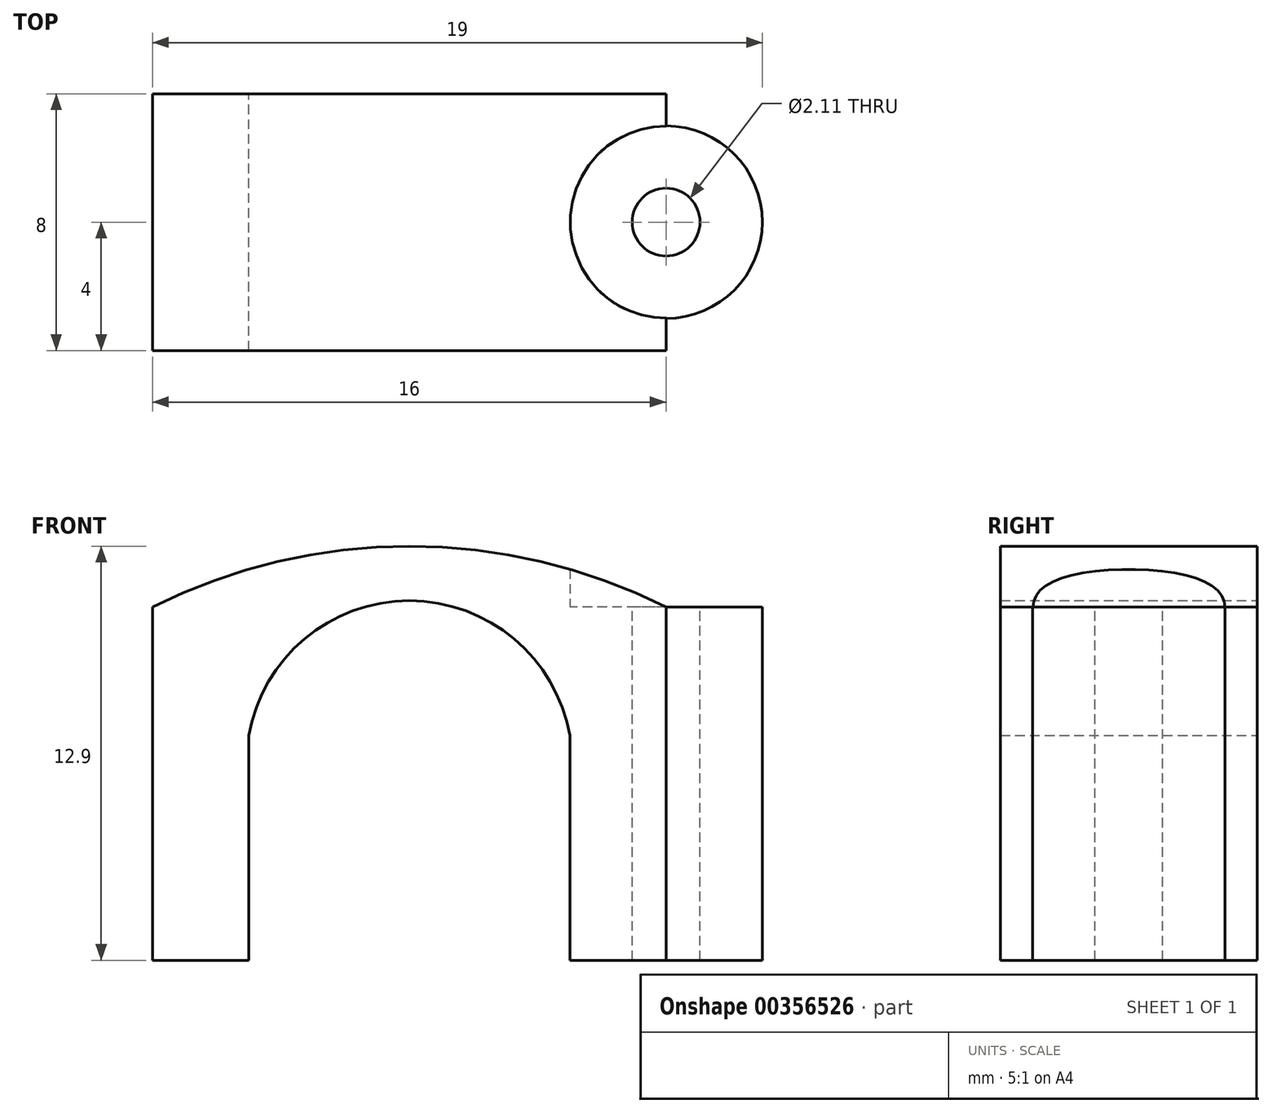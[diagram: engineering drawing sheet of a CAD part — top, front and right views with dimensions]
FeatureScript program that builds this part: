
annotation { "Feature Type Name" : "Feature", "Feature Type Description" : "" }
export const myFeature = defineFeature(function(context is Context, id is Id, definition is map)
    precondition{}
    {
        {
            var Q0;
            Q0=qCreatedBy(makeId("Top.planeOp"),FACE);
            var sketch = newSketch(context, id + "F0", { "sketchPlane" : qUnion([Q0])});
            skLineSegment(sketch, "E0.bottom", {"start": v(0, 0) * mm, "end": v(16, 0) * mm});
            skLineSegment(sketch, "E0.top", {"start": v(0, 8) * mm, "end": v(16, 8) * mm});
            skLineSegment(sketch, "E0.left", {"start": v(0, 0) * mm, "end": v(0, 8) * mm});
            skLineSegment(sketch, "E0.right", {"start": v(16, 0) * mm, "end": v(16, 8) * mm});
            skSolve(sketch);
        }
        {
            var Q0;
            Q0=makeQuery(id+"F0.imprint","IMPRINT",FACE,{"disambiguationData":[TD([[makeQuery(id+"F0.imprint","IMPRINT",EDGE,{"derivedFrom":sQuery(id+"F0.wireOp",EDGE,"E0.bottom")}),1.0]])]});
            extrude(context, id + "F1", {"entities" : qUnion([Q0]), "depth" : 11 * mm});
        }
        {
            var Q0;
            Q0=makeQuery(id+"F1.opExtrude","CAP_FACE",FACE,{"disambiguationData":[OSD([sQuery(id+"F0.wireOp",EDGE,"E0.bottom"),sQuery(id+"F0.wireOp",EDGE,"E0.top"),sQuery(id+"F0.wireOp",EDGE,"E0.left"),sQuery(id+"F0.wireOp",EDGE,"E0.right")])],"isStart":false});
            var sketch = newSketch(context, id + "F2", { "sketchPlane" : qUnion([Q0])});
            skLineSegment(sketch, "E1", {"start": v(16, 0) * mm, "end": v(16, 1) * mm});
            skLineSegment(sketch, "E2", {"start": v(16, 8) * mm, "end": v(16, 7) * mm});
            skCircle(sketch, "E3", {"center": v(16, 4) * mm, "radius": 3 * mm});
            skSolve(sketch);
        }
        {
            var Q0;
            {var subQ0=sQuery(id+"F2.wireOp",EDGE,"E3");var subQ1=makeQuery(id+"F1.opExtrude","CAP_EDGE",EDGE,{"disambiguationData":[OSD([sQuery(id+"F0.wireOp",EDGE,"E0.right")])],"isStart":false});var subQ2=makeQuery(id+"F2.imprint","INTERSECT",VERTEX,{"derivedFrom":[subQ1,sQuery(id+"F2.wireOp",EDGE,"E1"),subQ0]});Q0=makeQuery(id+"F2.imprint","IMPRINT",FACE,{"disambiguationData":[TD([[makeQuery(id+"F2.imprint","IMPRINT",EDGE,{"disambiguationData":[TD([[subQ2,-1.0]])],"derivedFrom":subQ0}),1.0]])]});}
            var Q1;
            {var subQ0=sQuery(id+"F2.wireOp",EDGE,"E3");var subQ1=makeQuery(id+"F1.opExtrude","CAP_EDGE",EDGE,{"disambiguationData":[OSD([sQuery(id+"F0.wireOp",EDGE,"E0.right")])],"isStart":false});var subQ2=makeQuery(id+"F2.imprint","INTERSECT",VERTEX,{"derivedFrom":[subQ1,sQuery(id+"F2.wireOp",EDGE,"E1"),subQ0]});Q1=makeQuery(id+"F2.imprint","IMPRINT",FACE,{"disambiguationData":[TD([[makeQuery(id+"F2.imprint","IMPRINT",EDGE,{"disambiguationData":[TD([[subQ2,1.0]])],"derivedFrom":subQ0}),1.0]])]});}
            extrude(context, id + "F3", {"entities" : qUnion([Q0, Q1]), "operationType" : NewBodyOperationType.ADD, "oppositeDirection" : true, "depth" : 11 * mm});
        }
        {
            var Q0;
            Q0=makeQuery(id+"F1.opExtrude","SWEPT_FACE",FACE,{"disambiguationData":[OSD([sQuery(id+"F0.wireOp",EDGE,"E0.top")])]});
            var sketch = newSketch(context, id + "F4", { "sketchPlane" : qUnion([Q0])});
            skArc(sketch, "E4", {"start": v(0, 11) * mm, "mid": v(-8, 12.9) * mm, "end": v(-16, 11) * mm});
            skSolve(sketch);
        }
        {
            var Q0;
            Q0=makeQuery(id+"F4.imprint","IMPRINT",FACE,{"disambiguationData":[TD([[makeQuery(id+"F4.imprint","IMPRINT",EDGE,{"derivedFrom":sQuery(id+"F4.wireOp",EDGE,"E4")}),1.0]])]});
            extrude(context, id + "F5", {"entities" : qUnion([Q0]), "operationType" : NewBodyOperationType.ADD, "oppositeDirection" : true, "depth" : 8 * mm});
        }
        {
            var Q0;
            {var subQ0=sQuery(id+"F0.wireOp",EDGE,"E0.top");Q0=makeQuery(id+"F5.boolean.opBoolean","MERGE",FACE,{"derivedFrom":[makeQuery(id+"F1.opExtrude","SWEPT_FACE",FACE,{"disambiguationData":[OSD([subQ0])]}),makeQuery(id+"F5.opExtrude","CAP_FACE",FACE,{"disambiguationData":[OSD([subQ0,sQuery(id+"F4.wireOp",EDGE,"E4")])],"isStart":true})]});}
            var sketch = newSketch(context, id + "F6", { "sketchPlane" : qUnion([Q0])});
            skLineSegment(sketch, "E5", {"start": v(0, 0) * mm, "end": v(-3, 0) * mm});
            skLineSegment(sketch, "E6", {"start": v(-16, 0) * mm, "end": v(-13, 0) * mm});
            skLineSegment(sketch, "E7.left", {"start": v(-13, 0) * mm, "end": v(-13, 0) * mm});
            skLineSegment(sketch, "E7.right", {"start": v(-3, 0) * mm, "end": v(-3, 0) * mm});
            skLineSegment(sketch, "E8.bottom", {"start": v(-13, 0) * mm, "end": v(-3, 0) * mm});
            skLineSegment(sketch, "E8.top", {"start": v(-13, 7) * mm, "end": v(-3, 7) * mm});
            skLineSegment(sketch, "E8.left", {"start": v(-13, 0) * mm, "end": v(-13, 7) * mm});
            skLineSegment(sketch, "E8.right", {"start": v(-3, 0) * mm, "end": v(-3, 7) * mm});
            skSolve(sketch);
        }
        {
            var Q0;
            Q0=makeQuery(id+"F6.imprint","IMPRINT",FACE,{"disambiguationData":[TD([[makeQuery(id+"F6.imprint","IMPRINT",EDGE,{"derivedFrom":sQuery(id+"F6.wireOp",EDGE,"E8.bottom")}),-1.0]])]});
            extrude(context, id + "F7", {"entities" : qUnion([Q0]), "operationType" : NewBodyOperationType.REMOVE, "oppositeDirection" : true, "depth" : 25.4 * mm});
        }
        {
            var Q0;
            {var subQ0=sQuery(id+"F0.wireOp",EDGE,"E0.top");Q0=makeQuery(id+"F5.boolean.opBoolean","MERGE",FACE,{"derivedFrom":[makeQuery(id+"F1.opExtrude","SWEPT_FACE",FACE,{"disambiguationData":[OSD([subQ0])]}),makeQuery(id+"F5.opExtrude","CAP_FACE",FACE,{"disambiguationData":[OSD([subQ0,sQuery(id+"F4.wireOp",EDGE,"E4")])],"isStart":true})]});}
            var sketch = newSketch(context, id + "F8", { "sketchPlane" : qUnion([Q0])});
            skArc(sketch, "E9", {"start": v(-3, 7) * mm, "mid": v(-8, 11.2) * mm, "end": v(-13, 7) * mm});
            skSolve(sketch);
        }
        {
            var Q0;
            Q0=makeQuery(id+"F8.imprint","IMPRINT",FACE,{"disambiguationData":[TD([[makeQuery(id+"F8.imprint","IMPRINT",EDGE,{"derivedFrom":sQuery(id+"F8.wireOp",EDGE,"E9")}),1.0]])]});
            extrude(context, id + "F9", {"entities" : qUnion([Q0]), "operationType" : NewBodyOperationType.REMOVE, "oppositeDirection" : true, "depth" : 25.4 * mm});
        }
        {
            var Q0;
            Q0=makeQuery(id+"F3.boolean.opBoolean","MERGE",FACE,{"derivedFrom":[makeQuery(id+"F1.opExtrude","CAP_FACE",FACE,{"disambiguationData":[OSD([sQuery(id+"F0.wireOp",EDGE,"E0.bottom"),sQuery(id+"F0.wireOp",EDGE,"E0.top"),sQuery(id+"F0.wireOp",EDGE,"E0.left"),sQuery(id+"F0.wireOp",EDGE,"E0.right")])],"isStart":false}),makeQuery(id+"F3.opExtrude","CAP_FACE",FACE,{"disambiguationData":[OSD([sQuery(id+"F2.wireOp",EDGE,"E3")])],"isStart":true})]});
            var sketch = newSketch(context, id + "F10", { "sketchPlane" : qUnion([Q0])});
            skCircle(sketch, "E10", {"center": v(16, 4) * mm, "radius": 3 * mm});
            skSolve(sketch);
        }
        {
            var Q0;
            Q0=qSketchRegion(id+"F10",true);
            extrude(context, id + "F11", {"entities" : qUnion([Q0]), "operationType" : NewBodyOperationType.REMOVE, "depth" : 25.4 * mm});
        }
        {
            var Q0;
            Q0=makeQuery(id+"F11.boolean.opBoolean","MERGE",FACE,{"derivedFrom":[makeQuery(id+"F3.boolean.opBoolean","MERGE",FACE,{"derivedFrom":[makeQuery(id+"F1.opExtrude","CAP_FACE",FACE,{"disambiguationData":[OSD([sQuery(id+"F0.wireOp",EDGE,"E0.bottom"),sQuery(id+"F0.wireOp",EDGE,"E0.top"),sQuery(id+"F0.wireOp",EDGE,"E0.left"),sQuery(id+"F0.wireOp",EDGE,"E0.right")])],"isStart":false}),makeQuery(id+"F3.opExtrude","CAP_FACE",FACE,{"disambiguationData":[OSD([sQuery(id+"F2.wireOp",EDGE,"E3")])],"isStart":true})]}),makeQuery(id+"F11.opExtrude","CAP_FACE",FACE,{"disambiguationData":[OSD([sQuery(id+"F10.wireOp",EDGE,"E10")])],"isStart":true})]});
            var sketch = newSketch(context, id + "F12", { "sketchPlane" : qUnion([Q0])});
            skCircle(sketch, "E11", {"center": v(16, 4) * mm, "radius": 1.06 * mm});
            skSolve(sketch);
        }
        {
            var Q0;
            Q0=makeQuery(id+"F12.imprint","IMPRINT",FACE,{"disambiguationData":[TD([[makeQuery(id+"F12.imprint","IMPRINT",EDGE,{"derivedFrom":sQuery(id+"F12.wireOp",EDGE,"E11")}),1.0]])]});
            extrude(context, id + "F13", {"entities" : qUnion([Q0]), "operationType" : NewBodyOperationType.REMOVE, "oppositeDirection" : true, "depth" : 25.4 * mm});
        }
    });
